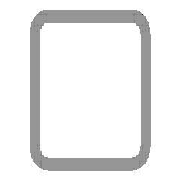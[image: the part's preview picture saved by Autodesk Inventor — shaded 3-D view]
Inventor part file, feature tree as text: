
AUTODESK INVENTOR PART (.ipt)
format: ipt  version: 2025.3 (Build 293356030, 356C)  size: 135,168 bytes
history: native  units: mm (DEFAULTED — no unit token found)
features: other x4, sketch x1, plane x1
ambient origin geometry x8: Origin, YZ Plane, XZ Plane, XY Plane, X Axis, Y Axis, Z Axis, Center Point
bodies: Solid1 (feature_tree), Body (feature_tree)
feature tree (6):
  parser-record x1  (decoder bookkeeping rows leaked as tree rows — omitted from the tree; the rows remain in map.json)
  other  "Driven Length"
  other  "Start Plane"
  other  "End Plane"
  sketch  "Sketch3"  dims[d3=180.0mm d4=0.0mm d7=4.0mm d9=40.0mm d11=40.0mm d12=2.0mm d13=40.0mm d14=220.0mm d15=20.0mm d16=20.0mm d17=90.0deg d18=180.0mm]
  plane  "Work Plane3"
